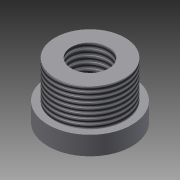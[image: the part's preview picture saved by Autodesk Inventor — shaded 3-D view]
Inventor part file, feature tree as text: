
AUTODESK INVENTOR PART (.ipt)
format: ipt  version: 2013 (Build 170138000, 138)  size: 100,864 bytes
history: native  units: in
note: dims shown in document units (in); Inventor stores cm internally (conversion verified against a paired STEP export)
features: extrude x2, thread x2, sketch x2
ambient origin geometry x8: Origin, YZ Plane, XZ Plane, XY Plane, X Axis, Y Axis, Z Axis, Center Point
bodies: Solid1 (feature_tree)
feature tree (6):
  extrude  "Extrusion1"  Depth=1.12in
  extrude  "Extrusion2"  Depth=0.937in
  thread  "Thread3"  [1 undecoded]
  thread  "Thread4"  [1 undecoded]
  sketch  "Sketch1"  dims[d0=0.5in d1=1.12in]
  sketch  "Sketch2"  dims[d2=0.75in d3=0.0in d6=0.937in d8=0.5in d9=0.0in d14=0.782in d15=0.0in d16=1.0in d17=0.0in]
note: 2 required parameter values undecoded (feature->parameter linkage not recoverable at this tier; creation-order binding heuristic only, values carry confidence <= 0.55)
